# Revit family: Sanitary_Showers_AXOR_28494000-AXOR-Starck-Plate-overhead-show
name_source: partatom
category: Plumbing Fixtures
revit_build: Autodesk Revit 2015 (Build: 20140606_1530(x64)
units: mm (PartAtom-declared; Revit-internal decimal feet)

## types (1)
- Chrome 000
    BIMobject category = Showers
    BIMobject category code = sanitary-showers
    BIMobject main category = Sanitary
    BIMobject main category code = sanitary
    BOSUseNativeGeometries = 1
    Brand url = https://www.axor-design.com
    Default Elevation = 4' - 0"
    Design country = Germany
    EAN code = https://4011097434025
    Edition number = 1
    IFC Classification = Sanitary Terminal
    Installation instructions = https://pro.hansgrohe-int.com
    Manufacturer country = Germany
    Manufacturer name = AXOR
    Material main = Chrome
    Product Guid = c274e66e-c20a-44b8-b47d-8de395dc0a0a
    Product SKU = 28494000
    Product data url = https://bimobject.com
    Product family = AXOR Starck
    Product group = Overhead showers
    Product name = AXOR Starck Plate overhead shower 240 1jet 28494000
    Product url = https://pro.hansgrohe-int.com
    QR code = http://bimobject.com
    Technical description = https://pro.hansgrohe-int.com

## geometry (parser evidence)
native form markers: Sweep x3
no freeform markers — native parametric forms only
